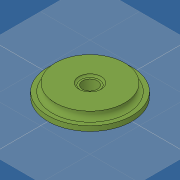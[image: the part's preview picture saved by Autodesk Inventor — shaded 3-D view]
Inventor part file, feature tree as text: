
AUTODESK INVENTOR PART (.ipt)
format: ipt  version: 2019 (Build 230136000, 136)  size: 131,584 bytes
history: native  units: mm
features: sketch x2, extrude x1, revolve x1, other x1
ambient origin geometry x8: Origin, YZ Plane, XZ Plane, XY Plane, X Axis, Y Axis, Z Axis, Center Point
bodies: Volumenkörper1 (feature_tree)
feature tree (5):
  extrude  "Extrusion1"  Depth=5.0mm TaperAngle=0.0deg
  revolve  "Umdrehung3"
  sketch  "Skizze1"  dims[d6=34.0mm d7=5.0mm d8=0.0mm]
  sketch  "Skizze4"  dims[d12=6.0mm d16=90.0deg d21=1.75mm d22=3.0mm d24=1.75mm d25=0.75mm d26=9.0mm]
  other  "Schnittkanten projizieren2"
